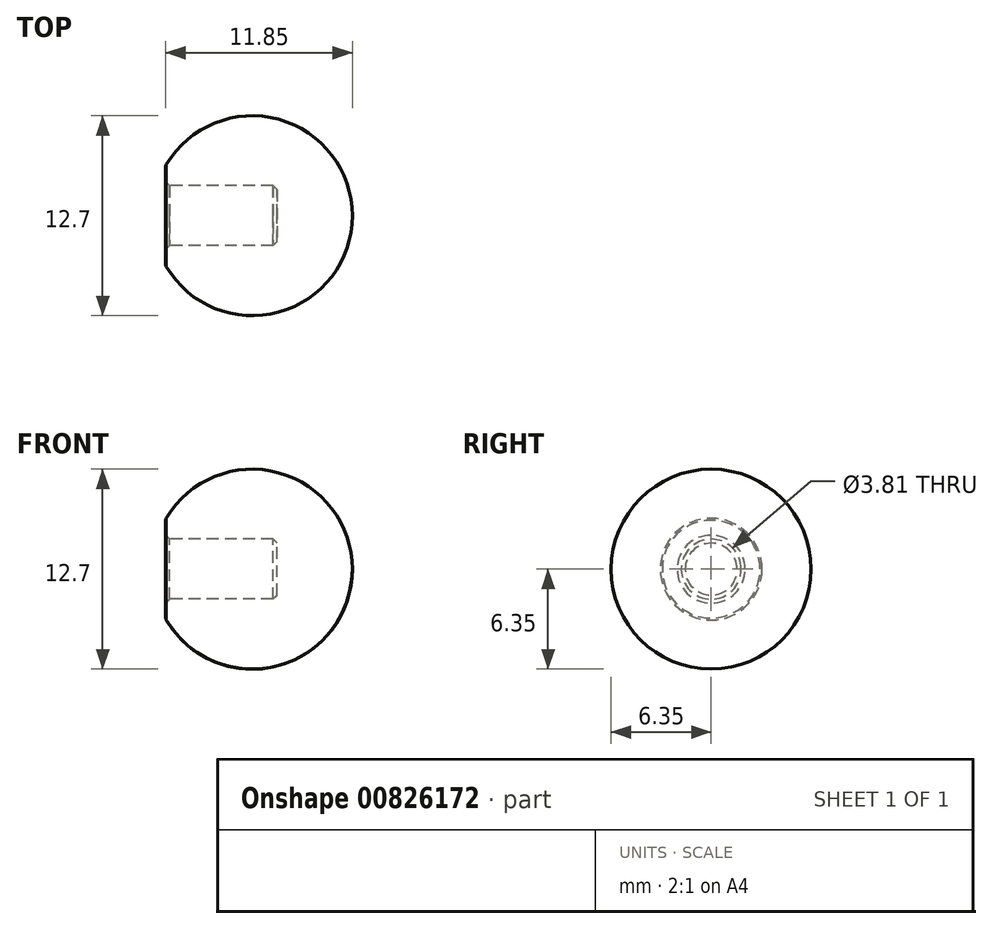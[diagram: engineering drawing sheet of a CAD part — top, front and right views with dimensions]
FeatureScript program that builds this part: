
annotation { "Feature Type Name" : "Feature", "Feature Type Description" : "" }
export const myFeature = defineFeature(function(context is Context, id is Id, definition is map)
    precondition{}
    {
        {
            var Q0;
            Q0=qCreatedBy(makeId("Front.planeOp"),FACE);
            var sketch = newSketch(context, id + "F0", { "sketchPlane" : qUnion([Q0])});
            skLineSegment(sketch, "E0", {"start": v(0, 0) * mm, "end": v(17.7, 0) * mm, "construction": true});
            skLineSegment(sketch, "E1", {"start": v(0, 1.9) * mm, "end": v(17.66, 1.9) * mm, "construction": true});
            skLineSegment(sketch, "E2", {"start": v(0, -1.9) * mm, "end": v(17.76, -1.9) * mm, "construction": true});
            skArc(sketch, "E3", {"start": v(0, -1.9) * mm, "mid": v(12.4, 0) * mm, "end": v(0, 1.9) * mm});
            skLineSegment(sketch, "E4", {"start": v(0, 1.9) * mm, "end": v(7.62, 1.9) * mm});
            skLineSegment(sketch, "E5", {"start": v(7.62, 1.9) * mm, "end": v(7.62, -1.9) * mm});
            skLineSegment(sketch, "E6", {"start": v(7.62, -1.9) * mm, "end": v(0, -1.9) * mm});
            skLineSegment(sketch, "E7", {"start": v(7.62, 0) * mm, "end": v(12.4, 0) * mm});
            skLineSegment(sketch, "E8", {"start": v(0, 3.18) * mm, "end": v(16.12, 3.18) * mm, "construction": true});
            skLineSegment(sketch, "E9", {"start": v(0.56, 3.18) * mm, "end": v(0.56, 0) * mm});
            skSolve(sketch);
        }
        {
            var Q0;
            {var subQ0=sQuery(id+"F0.wireOp",EDGE,"E7");Q0=makeQuery(id+"F0.imprint","IMPRINT",FACE,{"disambiguationData":[TD([[makeQuery(id+"F0.imprint","IMPRINT",EDGE,{"derivedFrom":subQ0}),1.0]])]});}
            var Q1;
            Q1=sQuery(id+"F0.wireOp",EDGE,"E0");
            revolve(context, id + "F1", {"surfaceOperationType" : NewSurfaceOperationType.NEW, "entities" : qUnion([Q0]), "axis" : qUnion([Q1]), "revolveType" : RevolveType.FULL});
        }
        {
            var Q0;
            Q0=makeQuery(id+"F1.opRevolve","SWEPT_EDGE",EDGE,{"disambiguationData":[OSD([sQuery(id+"F0.wireOp",EDGE,"E3"),sQuery(id+"F0.wireOp",EDGE,"E4")])]});
            chamfer(context, id + "F2", {"entities" : qUnion([Q0]), "width" : 0.25 * mm, "tangentPropagation" : true});
        }
    });
